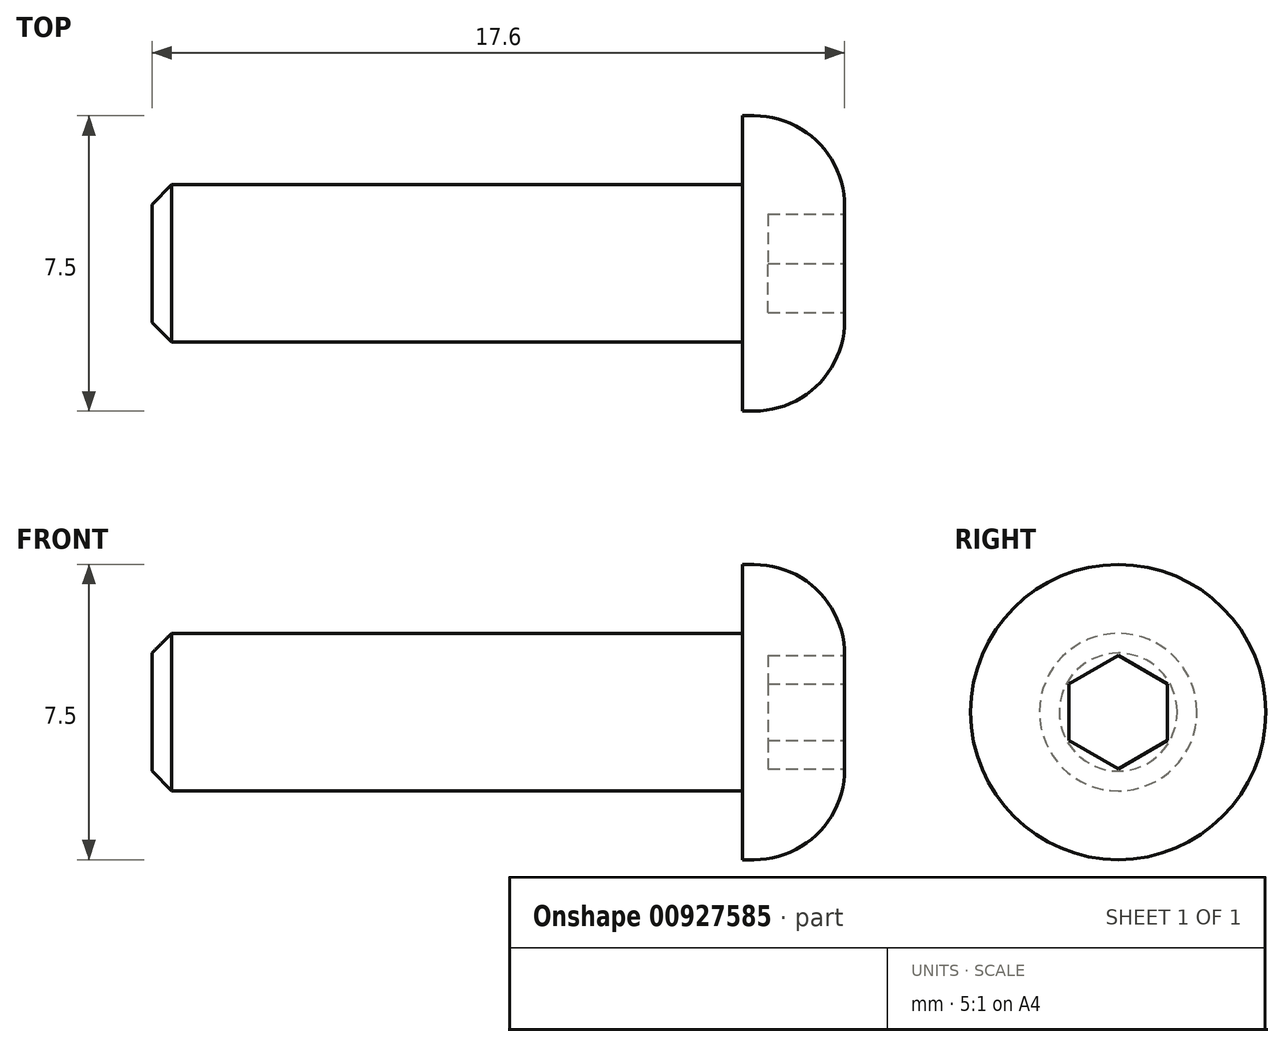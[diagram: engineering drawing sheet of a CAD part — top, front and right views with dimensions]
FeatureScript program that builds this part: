
annotation { "Feature Type Name" : "Feature", "Feature Type Description" : "" }
export const myFeature = defineFeature(function(context is Context, id is Id, definition is map)
    precondition{}
    {
        {
            var Q0;
            Q0=qCreatedBy(makeId("Right.planeOp"),FACE);
            var sketch = newSketch(context, id + "F0", { "sketchPlane" : qUnion([Q0])});
            skCircle(sketch, "E0", {"center": v(0, 0) * mm, "radius": 3.75 * mm});
            skSolve(sketch);
        }
        {
            var Q0;
            Q0 = qSketchRegion(id + "F0", true);
            extrude(context, id + "F1", {"entities" : qUnion([Q0]), "oppositeDirection" : true, "depth" : 2.6 * mm, "offsetDistance" : 25 * mm});
        }
        {
            var Q0;
            Q0=makeQuery(id+"F1.opExtrude","CAP_FACE",FACE,{"disambiguationData":[OSD([sQuery(id+"F0.wireOp",EDGE,"E0")])],"isStart":false});
            var sketch = newSketch(context, id + "F2", { "sketchPlane" : qUnion([Q0])});
            skCircle(sketch, "E1", {"center": v(0, 0) * mm, "radius": 2 * mm});
            skSolve(sketch);
        }
        {
            var Q0;
            Q0 = qSketchRegion(id + "F2", true);
            extrude(context, id + "F3", {"entities" : qUnion([Q0]), "operationType" : NewBodyOperationType.ADD, "depth" : 15 * mm, "offsetDistance" : 25 * mm});
        }
        {
            var Q0;
            Q0=makeQuery(id+"F3.opExtrude","CAP_EDGE",EDGE,{"disambiguationData":[OSD([sQuery(id+"F2.wireOp",EDGE,"E1")])],"isStart":false});
            chamfer(context, id + "F4", {"entities" : qUnion([Q0]), "width" : 0.5 * mm, "tangentPropagation" : true});
        }
        {
            var Q0;
            Q0=makeQuery(id+"F1.opExtrude","CAP_FACE",FACE,{"disambiguationData":[OSD([sQuery(id+"F0.wireOp",EDGE,"E0")])],"isStart":true});
            var sketch = newSketch(context, id + "F5", { "sketchPlane" : qUnion([Q0])});
            skLineSegment(sketch, "E2", {"start": v(0, 6.38) * mm, "end": v(0, -9.08) * mm, "construction": true});
            skLineSegment(sketch, "E3", {"start": v(-9.2, 0) * mm, "end": v(8.48, 0) * mm, "construction": true});
            skCircle(sketch, "E4.cCircle", {"center": v(0, 0) * mm, "radius": 1.25 * mm, "construction": true});
            skLineSegment(sketch, "E4.0", {"start": v(1.25, -0.72) * mm, "end": v(0, -1.44) * mm});
            skLineSegment(sketch, "E4.1", {"start": v(0, -1.44) * mm, "end": v(-1.25, -0.72) * mm});
            skLineSegment(sketch, "E4.2", {"start": v(-1.25, -0.72) * mm, "end": v(-1.25, 0.72) * mm});
            skLineSegment(sketch, "E4.3", {"start": v(-1.25, 0.72) * mm, "end": v(0, 1.44) * mm});
            skLineSegment(sketch, "E4.4", {"start": v(0, 1.44) * mm, "end": v(1.25, 0.72) * mm});
            skLineSegment(sketch, "E4.5", {"start": v(1.25, 0.72) * mm, "end": v(1.25, -0.72) * mm});
            skPoint(sketch, "E4.0.midPoint", {"position": v(0.62, -1.08) * mm});
            skSolve(sketch);
        }
        {
            var Q0;
            Q0 = qSketchRegion(id + "F5", true);
            extrude(context, id + "F6", {"entities" : qUnion([Q0]), "operationType" : NewBodyOperationType.REMOVE, "oppositeDirection" : true, "depth" : 1.95 * mm, "offsetDistance" : 25 * mm});
        }
        {
            var Q0;
            Q0=makeQuery(id+"F1.opExtrude","CAP_EDGE",EDGE,{"disambiguationData":[OSD([sQuery(id+"F0.wireOp",EDGE,"E0")])],"isStart":true});
            fillet(context, id + "F7", {"entities" : qUnion([Q0]), "radius" : 2.3 * mm, "tangentPropagation" : true, "allowEdgeOverflow" : false});
        }
    });
